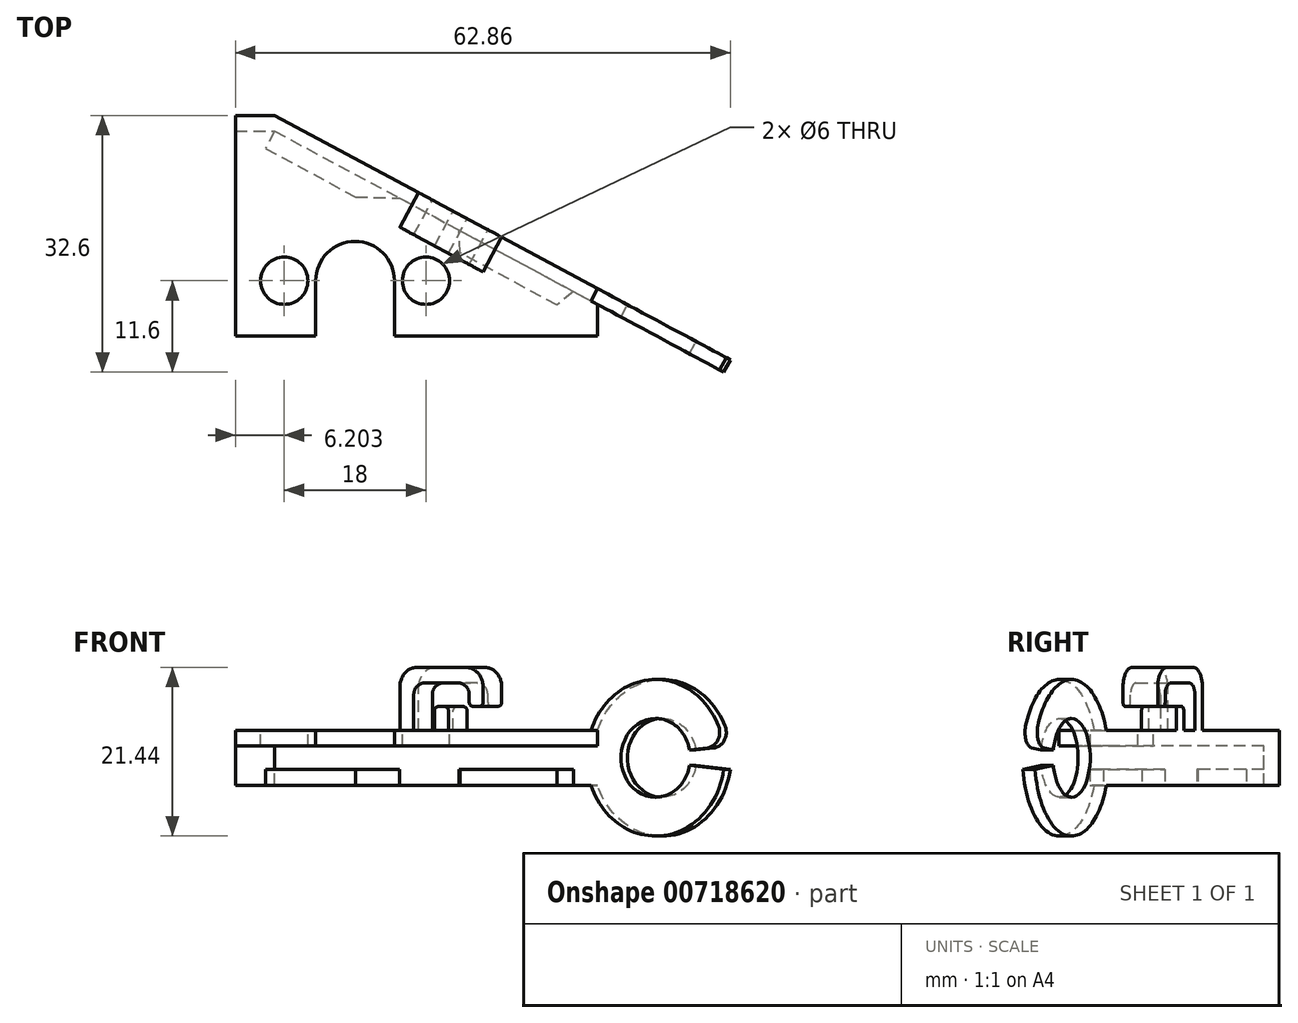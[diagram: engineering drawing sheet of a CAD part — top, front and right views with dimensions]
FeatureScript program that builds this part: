
annotation { "Feature Type Name" : "Feature", "Feature Type Description" : "" }
export const myFeature = defineFeature(function(context is Context, id is Id, definition is map)
    precondition{}
    {
        {
            var Q0;
            Q0=qCreatedBy(makeId("Top.planeOp"),FACE);
            var sketch = newSketch(context, id + "F0", { "sketchPlane" : qUnion([Q0])});
            skLineSegment(sketch, "E0", {"start": v(-19.75, 0) * mm, "end": v(26.25, 0) * mm});
            skLineSegment(sketch, "E1", {"start": v(26.25, 0) * mm, "end": v(26.25, 6) * mm});
            skLineSegment(sketch, "E2", {"start": v(26.25, 6) * mm, "end": v(-14.75, 28) * mm});
            skLineSegment(sketch, "E3", {"start": v(-14.75, 28) * mm, "end": v(-19.75, 28) * mm});
            skLineSegment(sketch, "E4", {"start": v(-19.75, 28) * mm, "end": v(-19.75, 0) * mm});
            skSolve(sketch);
        }
        {
            var Q0;
            Q0 = qSketchRegion(id + "F0", true);
            extrude(context, id + "F1", {"entities" : qUnion([Q0]), "depth" : 2 * mm, "offsetDistance" : 25 * mm});
        }
        {
            var Q0;
            Q0=makeQuery(id+"F1.opExtrude","CAP_FACE",FACE,{"disambiguationData":[OSD([sQuery(id+"F0.wireOp",EDGE,"E0"),sQuery(id+"F0.wireOp",EDGE,"E1"),sQuery(id+"F0.wireOp",EDGE,"E2"),sQuery(id+"F0.wireOp",EDGE,"E3"),sQuery(id+"F0.wireOp",EDGE,"E4")])],"isStart":false});
            var sketch = newSketch(context, id + "F2", { "sketchPlane" : qUnion([Q0])});
            skCircle(sketch, "E5", {"center": v(-13.55, 7) * mm, "radius": 3 * mm});
            skCircle(sketch, "E6", {"center": v(4.45, 7) * mm, "radius": 3 * mm});
            skPoint(sketch, "E7", {"position": v(-10.55, 7) * mm});
            skPoint(sketch, "E8", {"position": v(1.45, 7) * mm});
            skPoint(sketch, "E9", {"position": v(-16.55, 7) * mm});
            skPoint(sketch, "E10", {"position": v(-19.75, 7) * mm});
            skLineSegment(sketch, "E11", {"start": v(-9.55, 0) * mm, "end": v(-9.55, 7) * mm});
            skLineSegment(sketch, "E12", {"start": v(0.45, 0) * mm, "end": v(0.45, 7) * mm});
            skLineSegment(sketch, "E13", {"start": v(-9.55, 0) * mm, "end": v(0.45, 0) * mm});
            skLineSegment(sketch, "E14", {"start": v(-19.75, 7) * mm, "end": v(-16.55, 7) * mm, "construction": true});
            skLineSegment(sketch, "E15", {"start": v(-16.55, 7) * mm, "end": v(-10.55, 7) * mm, "construction": true});
            skPoint(sketch, "E16", {"position": v(-4.55, 7) * mm});
            skLineSegment(sketch, "E17", {"start": v(7.45, 7) * mm, "end": v(1.45, 7) * mm, "construction": true});
            skLineSegment(sketch, "E18", {"start": v(-10.55, 7) * mm, "end": v(-9.55, 7) * mm, "construction": true});
            skLineSegment(sketch, "E19", {"start": v(-9.55, 7) * mm, "end": v(-4.55, 7) * mm, "construction": true});
            skLineSegment(sketch, "E20", {"start": v(-4.55, 7) * mm, "end": v(0.45, 7) * mm, "construction": true});
            skLineSegment(sketch, "E21", {"start": v(0.45, 7) * mm, "end": v(1.45, 7) * mm, "construction": true});
            skLineSegment(sketch, "E22", {"start": v(-4.55, 7) * mm, "end": v(-4.55, 12) * mm, "construction": true});
            skArc(sketch, "E23", {"start": v(0.45, 7) * mm, "mid": v(-4.55, 12) * mm, "end": v(-9.55, 7) * mm});
            skSolve(sketch);
        }
        {
            var Q0;
            Q0 = qSketchRegion(id + "F2", true);
            extrude(context, id + "F3", {"entities" : qUnion([Q0]), "operationType" : NewBodyOperationType.REMOVE, "endBound" : BoundingType.UP_TO_NEXT, "oppositeDirection" : true, "depth" : 25 * mm, "offsetDistance" : 25 * mm});
        }
        {
            var Q0;
            Q0=makeQuery(id+"F1.opExtrude","SWEPT_FACE",FACE,{"disambiguationData":[OSD([sQuery(id+"F0.wireOp",EDGE,"E2")])]});
            var sketch = newSketch(context, id + "F4", { "sketchPlane" : qUnion([Q0])});
            skLineSegment(sketch, "E24", {"start": v(5.52, 2) * mm, "end": v(5.52, 10) * mm});
            skLineSegment(sketch, "E25", {"start": v(5.52, 10) * mm, "end": v(-6.48, 10) * mm});
            skLineSegment(sketch, "E26", {"start": v(-6.48, 10) * mm, "end": v(-6.48, 5.05) * mm});
            skLineSegment(sketch, "E27", {"start": v(-6.48, 5.05) * mm, "end": v(-4.48, 5.05) * mm});
            skLineSegment(sketch, "E28", {"start": v(-4.48, 5.05) * mm, "end": v(-4.48, 8) * mm});
            skLineSegment(sketch, "E29", {"start": v(-4.48, 8) * mm, "end": v(3.52, 8) * mm});
            skLineSegment(sketch, "E30", {"start": v(3.52, 8) * mm, "end": v(3.52, 2) * mm});
            skLineSegment(sketch, "E31", {"start": v(3.52, 2) * mm, "end": v(5.52, 2) * mm});
            skLineSegment(sketch, "E32.bottom", {"start": v(-1.48, 2) * mm, "end": v(0.52, 2) * mm});
            skLineSegment(sketch, "E32.top", {"start": v(-1.48, 5) * mm, "end": v(0.52, 5) * mm});
            skLineSegment(sketch, "E32.left", {"start": v(-1.48, 2) * mm, "end": v(-1.48, 5) * mm});
            skLineSegment(sketch, "E32.right", {"start": v(0.52, 2) * mm, "end": v(0.52, 5) * mm});
            skLineSegment(sketch, "E33", {"start": v(-4.48, 8) * mm, "end": v(-4.48, 10) * mm, "construction": true});
            skLineSegment(sketch, "E34", {"start": v(-0.48, 8) * mm, "end": v(-0.48, 5) * mm, "construction": true});
            skSolve(sketch);
        }
        {
            var Q0;
            Q0 = qSketchRegion(id + "F4", true);
            extrude(context, id + "F5", {"entities" : qUnion([Q0]), "operationType" : NewBodyOperationType.ADD, "oppositeDirection" : true, "depth" : 5 * mm, "offsetDistance" : 25 * mm});
        }
        {
            var Q0;
            Q0=makeQuery(id+"F5.opExtrude","SWEPT_EDGE",EDGE,{"disambiguationData":[OSD([sQuery(id+"F4.wireOp",EDGE,"E25"),sQuery(id+"F4.wireOp",EDGE,"E26")])]});
            var Q1;
            Q1=makeQuery(id+"F5.opExtrude","SWEPT_EDGE",EDGE,{"disambiguationData":[OSD([sQuery(id+"F4.wireOp",EDGE,"E24"),sQuery(id+"F4.wireOp",EDGE,"E25")])]});
            fillet(context, id + "F6", {"entities" : qUnion([Q0, Q1]), "radius" : 2.5 * mm, "tangentPropagation" : true, "allowEdgeOverflow" : false});
        }
        {
            var Q0;
            Q0=makeQuery(id+"F5.opExtrude","SWEPT_EDGE",EDGE,{"disambiguationData":[OSD([sQuery(id+"F0.wireOp",EDGE,"E2"),sQuery(id+"F4.wireOp",EDGE,"E32.bottom"),sQuery(id+"F4.wireOp",EDGE,"E32.right")])]});
            var Q1;
            Q1=makeQuery(id+"F5.opExtrude","SWEPT_EDGE",EDGE,{"disambiguationData":[OSD([sQuery(id+"F0.wireOp",EDGE,"E2"),sQuery(id+"F4.wireOp",EDGE,"E30"),sQuery(id+"F4.wireOp",EDGE,"E31")])]});
            var Q2;
            Q2=makeQuery(id+"F5.opExtrude","SWEPT_EDGE",EDGE,{"disambiguationData":[OSD([sQuery(id+"F4.wireOp",EDGE,"E28"),sQuery(id+"F4.wireOp",EDGE,"E29")])]});
            var Q3;
            Q3=makeQuery(id+"F5.opExtrude","SWEPT_EDGE",EDGE,{"disambiguationData":[OSD([sQuery(id+"F4.wireOp",EDGE,"E29"),sQuery(id+"F4.wireOp",EDGE,"E30")])]});
            fillet(context, id + "F7", {"entities" : qUnion([Q0, Q1, Q2, Q3]), "radius" : 1.5 * mm, "tangentPropagation" : true, "allowEdgeOverflow" : false});
        }
        {
            var Q0;
            Q0=makeQuery(id+"F5.opExtrude","SWEPT_EDGE",EDGE,{"disambiguationData":[OSD([sQuery(id+"F4.wireOp",EDGE,"E26"),sQuery(id+"F4.wireOp",EDGE,"E27")])]});
            var Q1;
            Q1=makeQuery(id+"F5.opExtrude","SWEPT_EDGE",EDGE,{"disambiguationData":[OSD([sQuery(id+"F4.wireOp",EDGE,"E27"),sQuery(id+"F4.wireOp",EDGE,"E28")])]});
            var Q2;
            Q2=makeQuery(id+"F5.opExtrude","SWEPT_EDGE",EDGE,{"disambiguationData":[OSD([sQuery(id+"F4.wireOp",EDGE,"E32.top"),sQuery(id+"F4.wireOp",EDGE,"E32.left")])]});
            var Q3;
            Q3=makeQuery(id+"F5.opExtrude","SWEPT_EDGE",EDGE,{"disambiguationData":[OSD([sQuery(id+"F4.wireOp",EDGE,"E32.top"),sQuery(id+"F4.wireOp",EDGE,"E32.right")])]});
            fillet(context, id + "F8", {"entities" : qUnion([Q0, Q1, Q2, Q3]), "radius" : 0.5 * mm, "tangentPropagation" : true, "allowEdgeOverflow" : false});
        }
        {
            var Q0;
            Q0=makeQuery(id+"F1.opExtrude","CAP_FACE",FACE,{"disambiguationData":[OSD([sQuery(id+"F0.wireOp",EDGE,"E0"),sQuery(id+"F0.wireOp",EDGE,"E1"),sQuery(id+"F0.wireOp",EDGE,"E2"),sQuery(id+"F0.wireOp",EDGE,"E3"),sQuery(id+"F0.wireOp",EDGE,"E4")])],"isStart":true});
            var sketch = newSketch(context, id + "F9", { "sketchPlane" : qUnion([Q0])});
            skLineSegment(sketch, "E35", {"start": v(-19.75, -28) * mm, "end": v(-19.75, -26) * mm});
            skLineSegment(sketch, "E36", {"start": v(-19.75, -26) * mm, "end": v(-14.75, -26) * mm});
            skLineSegment(sketch, "E37", {"start": v(-14.75, -26) * mm, "end": v(26.25, -4) * mm});
            skLineSegment(sketch, "E38", {"start": v(26.25, -4) * mm, "end": v(26.25, -6) * mm});
            skLineSegment(sketch, "E39", {"start": v(26.25, -6) * mm, "end": v(-14.75, -28) * mm});
            skLineSegment(sketch, "E40", {"start": v(-14.75, -28) * mm, "end": v(-19.75, -28) * mm});
            skSolve(sketch);
        }
        {
            var Q0;
            Q0 = qSketchRegion(id + "F9", true);
            extrude(context, id + "F10", {"entities" : qUnion([Q0]), "operationType" : NewBodyOperationType.ADD, "depth" : 5 * mm, "offsetDistance" : 25 * mm});
        }
        {
            var Q0;
            Q0=makeQuery(id+"F10.opExtrude","CAP_FACE",FACE,{"disambiguationData":[OSD([sQuery(id+"F9.wireOp",EDGE,"E35"),sQuery(id+"F9.wireOp",EDGE,"E36"),sQuery(id+"F9.wireOp",EDGE,"E37"),sQuery(id+"F9.wireOp",EDGE,"E38"),sQuery(id+"F9.wireOp",EDGE,"E39"),sQuery(id+"F9.wireOp",EDGE,"E40")])],"isStart":false});
            var sketch = newSketch(context, id + "F11", { "sketchPlane" : qUnion([Q0])});
            skLineSegment(sketch, "E41", {"start": v(-14.75, -26) * mm, "end": v(-15.93, -23.8) * mm});
            skLineSegment(sketch, "E42", {"start": v(-15.93, -23.8) * mm, "end": v(-4.47, -17.65) * mm});
            skLineSegment(sketch, "E43", {"start": v(-4.47, -17.65) * mm, "end": v(1.11, -17.49) * mm});
            skLineSegment(sketch, "E44", {"start": v(1.11, -17.49) * mm, "end": v(-14.75, -26) * mm});
            skLineSegment(sketch, "E45", {"start": v(23.17, -5.65) * mm, "end": v(21.1, -3.92) * mm});
            skLineSegment(sketch, "E46", {"start": v(21.1, -3.92) * mm, "end": v(8.77, -10.54) * mm});
            skLineSegment(sketch, "E47", {"start": v(8.77, -10.54) * mm, "end": v(8.63, -13.46) * mm});
            skLineSegment(sketch, "E48", {"start": v(8.63, -13.46) * mm, "end": v(23.17, -5.65) * mm});
            skLineSegment(sketch, "E49", {"start": v(8.77, -10.54) * mm, "end": v(9.95, -12.75) * mm, "construction": true});
            skSolve(sketch);
        }
        {
            var Q0;
            Q0 = qSketchRegion(id + "F11", true);
            extrude(context, id + "F12", {"entities" : qUnion([Q0]), "operationType" : NewBodyOperationType.ADD, "oppositeDirection" : true, "depth" : 2 * mm, "offsetDistance" : 25 * mm});
        }
        {
            var Q0;
            Q0=makeQuery(id+"F10.boolean.opBoolean","MERGE",FACE,{"derivedFrom":[makeQuery(id+"F5.boolean.opBoolean","MERGE",FACE,{"derivedFrom":[makeQuery(id+"F1.opExtrude","SWEPT_FACE",FACE,{"disambiguationData":[OSD([sQuery(id+"F0.wireOp",EDGE,"E2")])]}),makeQuery(id+"F5.opExtrude","CAP_FACE",FACE,{"disambiguationData":[OSD([sQuery(id+"F4.wireOp",EDGE,"E24"),sQuery(id+"F4.wireOp",EDGE,"E25"),sQuery(id+"F4.wireOp",EDGE,"E26"),sQuery(id+"F4.wireOp",EDGE,"E27"),sQuery(id+"F4.wireOp",EDGE,"E28"),sQuery(id+"F4.wireOp",EDGE,"E29"),sQuery(id+"F4.wireOp",EDGE,"E30"),sQuery(id+"F4.wireOp",EDGE,"E31")])],"isStart":true}),makeQuery(id+"F5.opExtrude","CAP_FACE",FACE,{"disambiguationData":[OSD([sQuery(id+"F4.wireOp",EDGE,"E32.bottom"),sQuery(id+"F4.wireOp",EDGE,"E32.top"),sQuery(id+"F4.wireOp",EDGE,"E32.left"),sQuery(id+"F4.wireOp",EDGE,"E32.right")])],"isStart":true})]}),makeQuery(id+"F10.opExtrude","SWEPT_FACE",FACE,{"disambiguationData":[OSD([sQuery(id+"F9.wireOp",EDGE,"E39")])]})]});
            var sketch = newSketch(context, id + "F13", { "sketchPlane" : qUnion([Q0])});
            skCircle(sketch, "E50", {"center": v(-29.6, -1.5) * mm, "radius": 9.94 * mm});
            skLineSegment(sketch, "E51", {"start": v(-20.3, -1.12) * mm, "end": v(-20.3, -1.5) * mm});
            skLineSegment(sketch, "E52", {"start": v(-20.3, -1.5) * mm, "end": v(-29.6, -1.5) * mm});
            skCircle(sketch, "E53", {"center": v(-29.6, -1.5) * mm, "radius": 5 * mm});
            skSolve(sketch);
        }
        {
            var Q0;
            Q0 = qSketchRegion(id + "F13", true);
            var Q1;
            Q1=makeQuery(id+"F10.opExtrude","SWEPT_FACE",FACE,{"disambiguationData":[OSD([sQuery(id+"F9.wireOp",EDGE,"E37")])]});
            extrude(context, id + "F14", {"entities" : qUnion([Q0]), "operationType" : NewBodyOperationType.ADD, "endBound" : BoundingType.UP_TO_SURFACE, "oppositeDirection" : true, "depth" : 25 * mm, "endBoundEntityFace" : qUnion([Q1]), "offsetDistance" : 25 * mm});
        }
        {
            var Q0;
            Q0=makeQuery(id+"F14.boolean.opBoolean","MERGE",FACE,{"derivedFrom":[makeQuery(id+"F10.boolean.opBoolean","MERGE",FACE,{"derivedFrom":[makeQuery(id+"F5.boolean.opBoolean","MERGE",FACE,{"derivedFrom":[makeQuery(id+"F1.opExtrude","SWEPT_FACE",FACE,{"disambiguationData":[OSD([sQuery(id+"F0.wireOp",EDGE,"E2")])]}),makeQuery(id+"F5.opExtrude","CAP_FACE",FACE,{"disambiguationData":[OSD([sQuery(id+"F4.wireOp",EDGE,"E24"),sQuery(id+"F4.wireOp",EDGE,"E25"),sQuery(id+"F4.wireOp",EDGE,"E26"),sQuery(id+"F4.wireOp",EDGE,"E27"),sQuery(id+"F4.wireOp",EDGE,"E28"),sQuery(id+"F4.wireOp",EDGE,"E29"),sQuery(id+"F4.wireOp",EDGE,"E30"),sQuery(id+"F4.wireOp",EDGE,"E31")])],"isStart":true}),makeQuery(id+"F5.opExtrude","CAP_FACE",FACE,{"disambiguationData":[OSD([sQuery(id+"F4.wireOp",EDGE,"E32.bottom"),sQuery(id+"F4.wireOp",EDGE,"E32.top"),sQuery(id+"F4.wireOp",EDGE,"E32.left"),sQuery(id+"F4.wireOp",EDGE,"E32.right")])],"isStart":true})]}),makeQuery(id+"F10.opExtrude","SWEPT_FACE",FACE,{"disambiguationData":[OSD([sQuery(id+"F9.wireOp",EDGE,"E39")])]})]}),makeQuery(id+"F14.opExtrude","CAP_FACE",FACE,{"disambiguationData":[OSD([sQuery(id+"F13.wireOp",EDGE,"E50"),sQuery(id+"F13.wireOp",EDGE,"E53")])],"isStart":true})]});
            var sketch = newSketch(context, id + "F15", { "sketchPlane" : qUnion([Q0])});
            skLineSegment(sketch, "E54", {"start": v(-34.5, -0.52) * mm, "end": v(-39.43, 0) * mm});
            skLineSegment(sketch, "E55", {"start": v(-34.5, -2.48) * mm, "end": v(-39.43, -3) * mm});
            skLineSegment(sketch, "E56", {"start": v(-20.3, 2) * mm, "end": v(-20.3, -5) * mm, "construction": true});
            skPoint(sketch, "E57", {"position": v(-20.3, -1.5) * mm});
            skLineSegment(sketch, "E58", {"start": v(-20.3, -1.5) * mm, "end": v(-39.54, -1.5) * mm, "construction": true});
            skArc(sketch, "E59", {"start": v(-39.43, 0) * mm, "mid": v(-39.54, -1.5) * mm, "end": v(-39.43, -3) * mm});
            skPoint(sketch, "E60", {"position": v(-34.6, -1.5) * mm});
            skArc(sketch, "E61", {"start": v(-34.5, -0.52) * mm, "mid": v(-34.6, -1.5) * mm, "end": v(-34.5, -2.48) * mm});
            skSolve(sketch);
        }
        {
            var Q0;
            Q0 = qSketchRegion(id + "F15", true);
            extrude(context, id + "F16", {"entities" : qUnion([Q0]), "operationType" : NewBodyOperationType.REMOVE, "endBound" : BoundingType.UP_TO_NEXT, "oppositeDirection" : true, "depth" : 25 * mm, "offsetDistance" : 25 * mm});
        }
        {
            var Q0;
            Q0=makeQuery(id+"F16.boolean.opBoolean","COPY",EDGE,{"derivedFrom":makeQuery(id+"F16.opExtrude","SWEPT_EDGE",EDGE,{"disambiguationData":[OSD([sQuery(id+"F13.wireOp",EDGE,"E50"),sQuery(id+"F15.wireOp",EDGE,"E55"),sQuery(id+"F15.wireOp",EDGE,"E59")])]})});
            var Q1;
            Q1=makeQuery(id+"F16.boolean.opBoolean","COPY",EDGE,{"derivedFrom":makeQuery(id+"F16.opExtrude","SWEPT_EDGE",EDGE,{"disambiguationData":[OSD([sQuery(id+"F13.wireOp",EDGE,"E50"),sQuery(id+"F15.wireOp",EDGE,"E54"),sQuery(id+"F15.wireOp",EDGE,"E59")])]})});
            var Q2;
            Q2=makeQuery(id+"F16.boolean.opBoolean","COPY",EDGE,{"derivedFrom":makeQuery(id+"F16.opExtrude","SWEPT_EDGE",EDGE,{"disambiguationData":[OSD([sQuery(id+"F13.wireOp",EDGE,"E53"),sQuery(id+"F15.wireOp",EDGE,"E54"),sQuery(id+"F15.wireOp",EDGE,"E61")])]})});
            var Q3;
            Q3=makeQuery(id+"F16.boolean.opBoolean","COPY",EDGE,{"derivedFrom":makeQuery(id+"F16.opExtrude","SWEPT_EDGE",EDGE,{"disambiguationData":[OSD([sQuery(id+"F13.wireOp",EDGE,"E53"),sQuery(id+"F15.wireOp",EDGE,"E55"),sQuery(id+"F15.wireOp",EDGE,"E61")])]})});
            fillet(context, id + "F17", {"entities" : qUnion([Q0, Q1, Q2, Q3]), "radius" : 2 * mm, "tangentPropagation" : true, "allowEdgeOverflow" : false});
        }
    });
